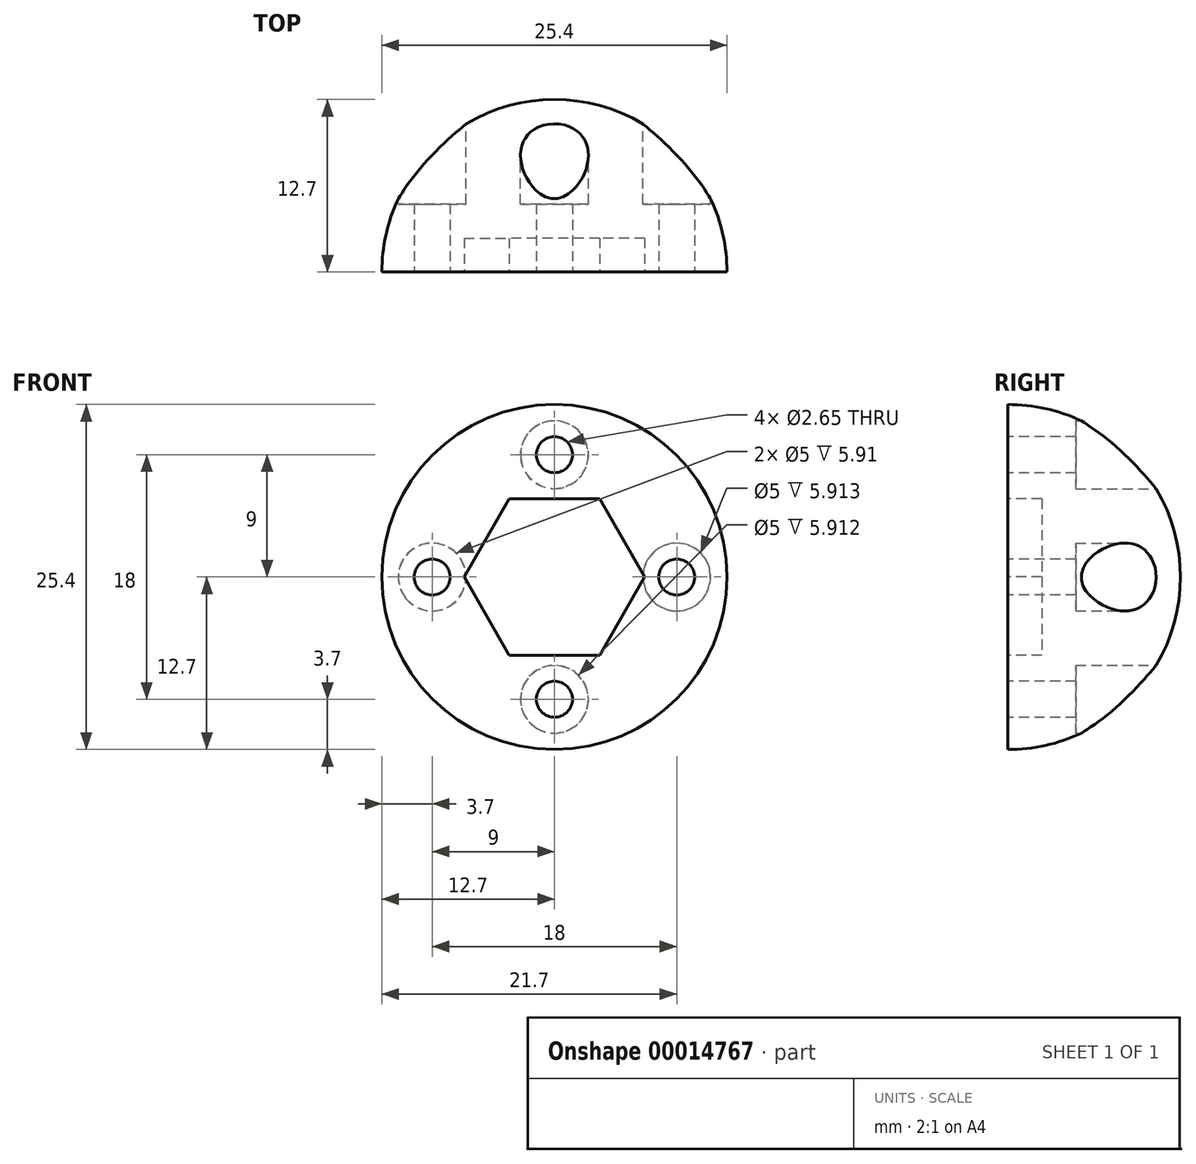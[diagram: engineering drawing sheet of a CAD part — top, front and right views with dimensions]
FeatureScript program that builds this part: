
annotation { "Feature Type Name" : "Feature", "Feature Type Description" : "" }
export const myFeature = defineFeature(function(context is Context, id is Id, definition is map)
    precondition{}
    {
        {
            var Q0;
            Q0=qCreatedBy(makeId("Top.planeOp"),FACE);
            var sketch = newSketch(context, id + "F0", { "sketchPlane" : qUnion([Q0])});
            skArc(sketch, "E0", {"start": v(12.7, 0) * mm, "mid": v(0, 12.7) * mm, "end": v(-12.7, 0) * mm});
            skLineSegment(sketch, "E1", {"start": v(-12.7, 0) * mm, "end": v(12.7, 0) * mm});
            skSolve(sketch);
        }
        {
            var Q0;
            Q0=makeQuery(id+"F0.imprint","IMPRINT",FACE,{"disambiguationData":[TD([[makeQuery(id+"F0.imprint","IMPRINT",EDGE,{"derivedFrom":sQuery(id+"F0.wireOp",EDGE,"E0")}),1.0]])]});
            var Q1;
            Q1=sQuery(id+"F0.wireOp",EDGE,"E1");
            revolve(context, id + "F1", {"entities" : qUnion([Q0]), "axis" : qUnion([Q1]), "revolveType" : RevolveType.TWO_DIRECTIONS, "oppositeDirection" : true, "angle" : 90 * degree, "angleBack" : 270 * degree});
        }
        {
            var Q0;
            Q0=qCreatedBy(makeId("Front.planeOp"),FACE);
            var sketch = newSketch(context, id + "F2", { "sketchPlane" : qUnion([Q0])});
            skCircle(sketch, "E2.cCircle", {"center": v(0, 0) * mm, "radius": 5.75 * mm, "construction": true});
            skLineSegment(sketch, "E2.0", {"start": v(3.32, -5.75) * mm, "end": v(-3.32, -5.75) * mm});
            skLineSegment(sketch, "E2.1", {"start": v(-3.32, -5.75) * mm, "end": v(-6.64, 0) * mm});
            skLineSegment(sketch, "E2.2", {"start": v(-6.64, 0) * mm, "end": v(-3.32, 5.75) * mm});
            skLineSegment(sketch, "E2.3", {"start": v(-3.32, 5.75) * mm, "end": v(3.32, 5.75) * mm});
            skLineSegment(sketch, "E2.4", {"start": v(3.32, 5.75) * mm, "end": v(6.64, 0) * mm});
            skLineSegment(sketch, "E2.5", {"start": v(6.64, 0) * mm, "end": v(3.32, -5.75) * mm});
            skPoint(sketch, "E2.0.midPoint", {"position": v(0, -5.75) * mm});
            skSolve(sketch);
        }
        {
            var Q0;
            Q0=makeQuery(id+"F2.imprint","IMPRINT",FACE,{"disambiguationData":[TD([[makeQuery(id+"F2.imprint","IMPRINT",EDGE,{"derivedFrom":sQuery(id+"F2.wireOp",EDGE,"E2.0")}),-1.0]])]});
            extrude(context, id + "F3", {"entities" : qUnion([Q0]), "operationType" : NewBodyOperationType.REMOVE, "oppositeDirection" : true, "depth" : 2.5 * mm});
        }
        {
            var Q0;
            Q0=qCreatedBy(makeId("Front.planeOp"),FACE);
            var sketch = newSketch(context, id + "F4", { "sketchPlane" : qUnion([Q0])});
            skCircle(sketch, "E3", {"center": v(0, 9) * mm, "radius": 1.32 * mm});
            skCircle(sketch, "E4", {"center": v(9, 0) * mm, "radius": 1.32 * mm});
            skCircle(sketch, "E5", {"center": v(0, -9) * mm, "radius": 1.32 * mm});
            skCircle(sketch, "E6", {"center": v(-9, 0) * mm, "radius": 1.32 * mm});
            skSolve(sketch);
        }
        {
            var Q0;
            Q0=makeQuery(id+"F4.imprint","IMPRINT",FACE,{"disambiguationData":[TD([[makeQuery(id+"F4.imprint","IMPRINT",EDGE,{"derivedFrom":sQuery(id+"F4.wireOp",EDGE,"E3")}),1.0]])]});
            var Q1;
            Q1=makeQuery(id+"F4.imprint","IMPRINT",FACE,{"disambiguationData":[TD([[makeQuery(id+"F4.imprint","IMPRINT",EDGE,{"derivedFrom":sQuery(id+"F4.wireOp",EDGE,"E4")}),1.0]])]});
            var Q2;
            Q2=makeQuery(id+"F4.imprint","IMPRINT",FACE,{"disambiguationData":[TD([[makeQuery(id+"F4.imprint","IMPRINT",EDGE,{"derivedFrom":sQuery(id+"F4.wireOp",EDGE,"E5")}),1.0]])]});
            var Q3;
            Q3=makeQuery(id+"F4.imprint","IMPRINT",FACE,{"disambiguationData":[TD([[makeQuery(id+"F4.imprint","IMPRINT",EDGE,{"derivedFrom":sQuery(id+"F4.wireOp",EDGE,"E6")}),1.0]])]});
            extrude(context, id + "F5", {"entities" : qUnion([Q0, Q1, Q2, Q3]), "operationType" : NewBodyOperationType.REMOVE, "endBound" : BoundingType.THROUGH_ALL, "oppositeDirection" : true, "depth" : 25 * mm});
        }
        {
            var Q0;
            Q0=qCreatedBy(makeId("Front.planeOp"),FACE);
            cPlane(context, id + "F6", {"entities" : qUnion([Q0]), "cplaneType" : CPlaneType.OFFSET, "offset" : 5 * mm, "oppositeDirection" : true, "width" : 150 * mm, "height" : 150 * mm});
        }
        {
            var Q0;
            Q0=qCreatedBy(makeId("Front.planeOp"),FACE);
            cPlane(context, id + "F7", {"entities" : qUnion([Q0]), "cplaneType" : CPlaneType.OFFSET, "offset" : 12.7 * mm, "oppositeDirection" : true, "width" : 150 * mm, "height" : 150 * mm});
        }
        {
            var Q0;
            Q0=qCreatedBy(id+"F7.planeOp",FACE);
            var sketch = newSketch(context, id + "F8", { "sketchPlane" : qUnion([Q0])});
            skCircle(sketch, "E7", {"center": v(0, 9) * mm, "radius": 2.5 * mm});
            skCircle(sketch, "E8", {"center": v(-9, 0) * mm, "radius": 2.5 * mm});
            skCircle(sketch, "E9", {"center": v(0, -9) * mm, "radius": 2.5 * mm});
            skCircle(sketch, "E10", {"center": v(9, 0) * mm, "radius": 2.5 * mm});
            skSolve(sketch);
        }
        {
            var Q0;
            Q0=makeQuery(id+"F8.imprint","IMPRINT",FACE,{"disambiguationData":[TD([[makeQuery(id+"F8.imprint","IMPRINT",EDGE,{"derivedFrom":sQuery(id+"F8.wireOp",EDGE,"E7")}),1.0]])]});
            var Q1;
            Q1=makeQuery(id+"F8.imprint","IMPRINT",FACE,{"disambiguationData":[TD([[makeQuery(id+"F8.imprint","IMPRINT",EDGE,{"derivedFrom":sQuery(id+"F8.wireOp",EDGE,"E10")}),1.0]])]});
            var Q2;
            Q2=makeQuery(id+"F8.imprint","IMPRINT",FACE,{"disambiguationData":[TD([[makeQuery(id+"F8.imprint","IMPRINT",EDGE,{"derivedFrom":sQuery(id+"F8.wireOp",EDGE,"E8")}),1.0]])]});
            var Q3;
            Q3=makeQuery(id+"F8.imprint","IMPRINT",FACE,{"disambiguationData":[TD([[makeQuery(id+"F8.imprint","IMPRINT",EDGE,{"derivedFrom":sQuery(id+"F8.wireOp",EDGE,"E9")}),1.0]])]});
            extrude(context, id + "F9", {"entities" : qUnion([Q0, Q1, Q2, Q3]), "operationType" : NewBodyOperationType.REMOVE, "depth" : 7.7 * mm});
        }
    });
